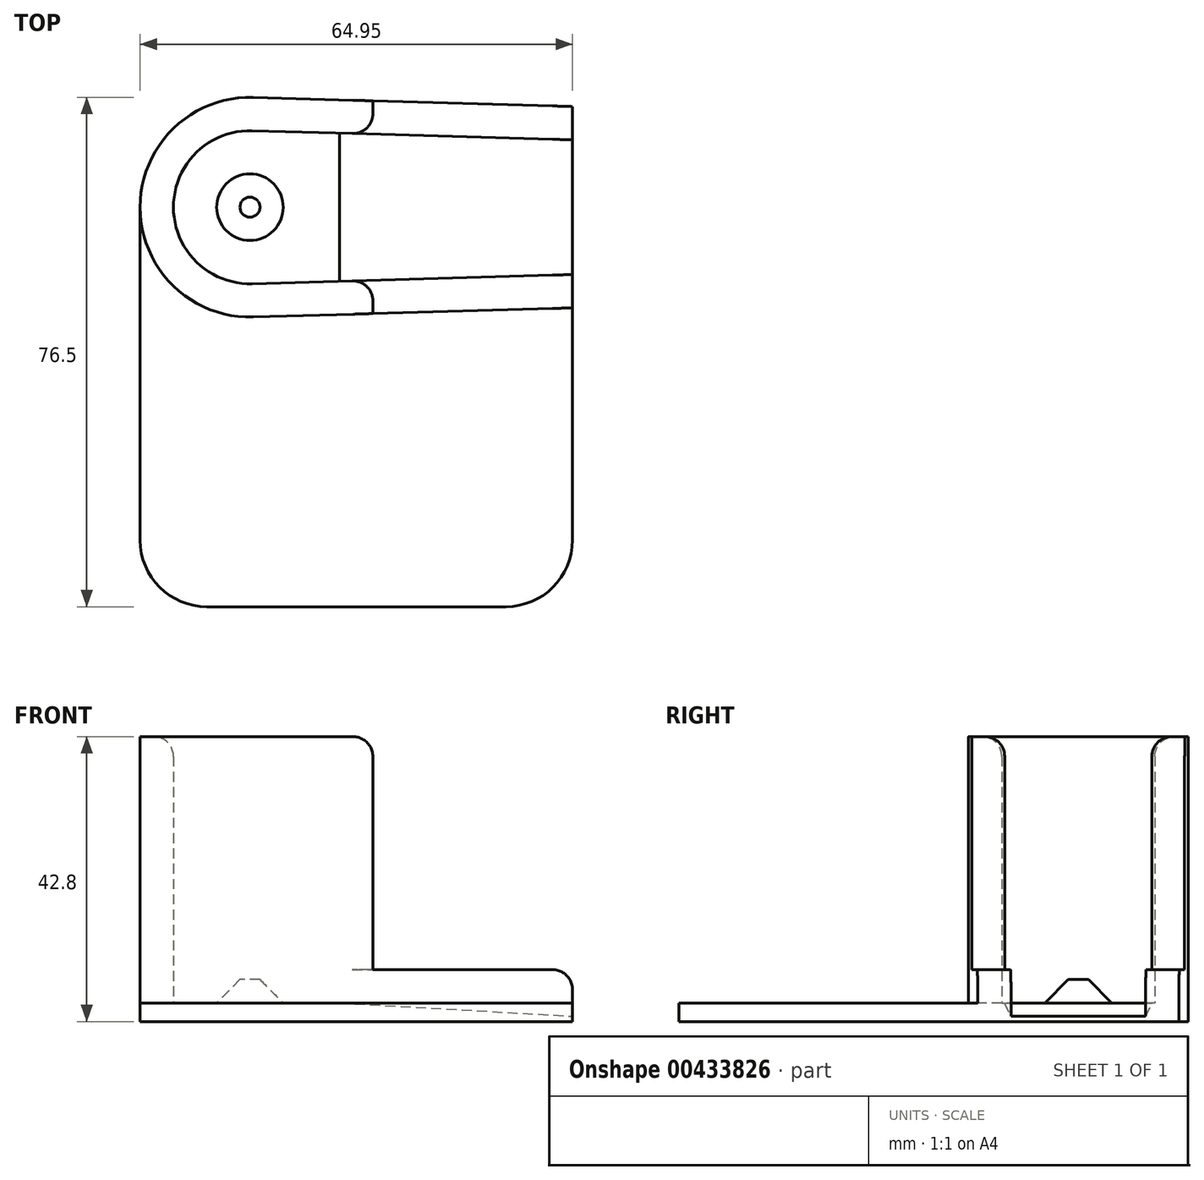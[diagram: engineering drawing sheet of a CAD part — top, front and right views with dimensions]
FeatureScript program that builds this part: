
annotation { "Feature Type Name" : "Feature", "Feature Type Description" : "" }
export const myFeature = defineFeature(function(context is Context, id is Id, definition is map)
    precondition{}
    {
        {
            var Q0;
            Q0=qCreatedBy(makeId("Top.planeOp"),FACE);
            var sketch = newSketch(context, id + "F0", { "sketchPlane" : qUnion([Q0])});
            skArc(sketch, "E0", {"start": v(0.54, 9.48) * mm, "mid": v(-9.5, 0.14) * mm, "end": v(0.27, -9.5) * mm, "construction": true});
            skCircle(sketch, "E1", {"center": v(122.1, 0) * mm, "radius": 6 * mm, "construction": true});
            skLineSegment(sketch, "E2", {"start": v(-9.5, 0) * mm, "end": v(128.1, 0) * mm, "construction": true});
            skLineSegment(sketch, "E3", {"start": v(0, 9.5) * mm, "end": v(122.27, 6) * mm, "construction": true});
            skLineSegment(sketch, "E4", {"start": v(122.27, -6) * mm, "end": v(0, -9.5) * mm, "construction": true});
            skArc(sketch, "E5.0", {"start": v(0.33, 11.5) * mm, "mid": v(-11.5, 0) * mm, "end": v(0.33, -11.5) * mm});
            skCircle(sketch, "E6.0", {"center": v(122.1, 0) * mm, "radius": 8 * mm, "construction": true});
            skLineSegment(sketch, "E7", {"start": v(0.33, 11.5) * mm, "end": v(18.47, 10.98) * mm});
            skLineSegment(sketch, "E8.MirrorCS", {"start": v(0.33, -11.5) * mm, "end": v(18.47, -10.98) * mm});
            skLineSegment(sketch, "E9.0", {"start": v(0.47, 16.5) * mm, "end": v(18.47, 15.98) * mm});
            skArc(sketch, "E9.1", {"start": v(0.47, 16.5) * mm, "mid": v(-16.5, 0) * mm, "end": v(0.47, -16.5) * mm});
            skLineSegment(sketch, "E9.2", {"start": v(0.47, -16.5) * mm, "end": v(18.47, -15.98) * mm});
            skLineSegment(sketch, "E10", {"start": v(18.47, 15.98) * mm, "end": v(18.47, -15.98) * mm, "construction": true});
            skLineSegment(sketch, "E11", {"start": v(18.47, 15.98) * mm, "end": v(18.47, 10.98) * mm});
            skLineSegment(sketch, "E12.MirrorCS", {"start": v(18.47, -15.98) * mm, "end": v(18.47, -10.98) * mm});
            skPoint(sketch, "E13.orphan", {"position": v(122.33, -8) * mm});
            skPoint(sketch, "E14.orphan", {"position": v(122.33, 8) * mm});
            skLineSegment(sketch, "E15", {"start": v(18.47, -15.98) * mm, "end": v(48.45, -15.12) * mm});
            skLineSegment(sketch, "E16", {"start": v(48.45, -15.12) * mm, "end": v(48.45, -10.12) * mm});
            skLineSegment(sketch, "E17", {"start": v(48.45, -10.12) * mm, "end": v(18.47, -10.98) * mm});
            skLineSegment(sketch, "E18.MirrorCS", {"start": v(48.45, 10.12) * mm, "end": v(18.47, 10.98) * mm});
            skLineSegment(sketch, "E19.MirrorCS", {"start": v(18.47, 15.98) * mm, "end": v(48.45, 15.12) * mm});
            skLineSegment(sketch, "E20.MirrorCS", {"start": v(48.45, 15.12) * mm, "end": v(48.45, 10.12) * mm});
            skLineSegment(sketch, "E21", {"start": v(-16.5, 0) * mm, "end": v(-16.5, -50) * mm});
            skLineSegment(sketch, "E22", {"start": v(-6.5, -60) * mm, "end": v(38.45, -60) * mm});
            skLineSegment(sketch, "E23", {"start": v(48.45, -50) * mm, "end": v(48.45, -15.12) * mm});
            skPoint(sketch, "E24.visualSharp", {"position": v(-16.5, -60) * mm});
            skArc(sketch, "E24.filletArc", {"start": v(-16.5, -50) * mm, "mid": v(-13.57, -57.07) * mm, "end": v(-6.5, -60) * mm});
            skPoint(sketch, "E25.visualSharp", {"position": v(48.45, -60) * mm});
            skArc(sketch, "E25.filletArc", {"start": v(38.45, -60) * mm, "mid": v(45.52, -57.07) * mm, "end": v(48.45, -50) * mm});
            skLineSegment(sketch, "E26", {"start": v(48.45, -10.12) * mm, "end": v(48.45, 10.12) * mm});
            skSolve(sketch);
        }
        {
            var Q0;
            Q0=makeQuery(id+"F0.imprint","IMPRINT",FACE,{"disambiguationData":[TD([[makeQuery(id+"F0.imprint","IMPRINT",EDGE,{"derivedFrom":sQuery(id+"F0.wireOp",EDGE,"E5.0")}),-1.0]])]});
            extrude(context, id + "F1", {"entities" : qUnion([Q0]), "depth" : 40 * mm});
        }
        {
            var Q0;
            Q0=makeQuery(id+"F0.imprint","IMPRINT",FACE,{"disambiguationData":[TD([[makeQuery(id+"F0.imprint","IMPRINT",EDGE,{"derivedFrom":sQuery(id+"F0.wireOp",EDGE,"E11")}),1.0]])]});
            var Q1;
            Q1=makeQuery(id+"F0.imprint","IMPRINT",FACE,{"disambiguationData":[TD([[makeQuery(id+"F0.imprint","IMPRINT",EDGE,{"derivedFrom":sQuery(id+"F0.wireOp",EDGE,"E12.MirrorCS")}),-1.0]])]});
            extrude(context, id + "F2", {"entities" : qUnion([Q0, Q1]), "operationType" : NewBodyOperationType.ADD, "depth" : 5 * mm});
        }
        {
            var Q0;
            Q0 = qSketchRegion(id + "F0", true);
            extrude(context, id + "F3", {"entities" : qUnion([Q0]), "operationType" : NewBodyOperationType.ADD, "oppositeDirection" : true, "depth" : 2.8 * mm});
        }
        {
            var Q0;
            Q0=makeQuery(id+"F0.imprint","IMPRINT",FACE,{"disambiguationData":[TD([[makeQuery(id+"F0.imprint","IMPRINT",EDGE,{"derivedFrom":sQuery(id+"F0.wireOp",EDGE,"E5.0")}),1.0]])]});
            var sketch = newSketch(context, id + "F4", { "sketchPlane" : qUnion([Q0])});
            skCircle(sketch, "E27", {"center": v(0, 0) * mm, "radius": 5 * mm});
            skSolve(sketch);
        }
        {
            var Q0;
            Q0=makeQuery(id+"F4.imprint","IMPRINT",FACE,{"disambiguationData":[TD([[makeQuery(id+"F4.imprint","IMPRINT",EDGE,{"derivedFrom":sQuery(id+"F4.wireOp",EDGE,"E27")}),1.0]])]});
            extrude(context, id + "F5", {"entities" : qUnion([Q0]), "operationType" : NewBodyOperationType.ADD, "depth" : 3.5 * mm, "hasDraft" : true, "draftAngle" : 45 * degree, "draftPullDirection" : true});
        }
        {
            var Q0;
            Q0=makeQuery(id+"F1.opExtrude","CAP_EDGE",EDGE,{"disambiguationData":[OSD([sQuery(id+"F0.wireOp",EDGE,"E12.MirrorCS")])],"isStart":false});
            var Q1;
            Q1=makeQuery(id+"F2.opExtrude","CAP_EDGE",EDGE,{"disambiguationData":[OSD([sQuery(id+"F0.wireOp",EDGE,"E12.MirrorCS")])],"isStart":false});
            var Q2;
            Q2=makeQuery(id+"F1.opExtrude","CAP_EDGE",EDGE,{"disambiguationData":[OSD([sQuery(id+"F0.wireOp",EDGE,"E11")])],"isStart":false});
            var Q3;
            Q3=makeQuery(id+"F2.opExtrude","CAP_EDGE",EDGE,{"disambiguationData":[OSD([sQuery(id+"F0.wireOp",EDGE,"E11")])],"isStart":false});
            var Q4;
            Q4=makeQuery(id+"F2.opExtrude","CAP_EDGE",EDGE,{"disambiguationData":[OSD([sQuery(id+"F0.wireOp",EDGE,"E16")])],"isStart":false});
            var Q5;
            Q5=makeQuery(id+"F2.opExtrude","CAP_EDGE",EDGE,{"disambiguationData":[OSD([sQuery(id+"F0.wireOp",EDGE,"E20.MirrorCS")])],"isStart":false});
            var Q6;
            Q6=makeQuery(id+"F1.opExtrude","SWEPT_EDGE",EDGE,{"disambiguationData":[OSD([sQuery(id+"F0.wireOp",EDGE,"E8.MirrorCS"),sQuery(id+"F0.wireOp",EDGE,"E12.MirrorCS"),sQuery(id+"F0.wireOp",EDGE,"E17")])]});
            var Q7;
            Q7=makeQuery(id+"F1.opExtrude","CAP_EDGE",EDGE,{"disambiguationData":[OSD([sQuery(id+"F0.wireOp",EDGE,"E8.MirrorCS")])],"isStart":false});
            var Q8;
            Q8=makeQuery(id+"F1.opExtrude","SWEPT_EDGE",EDGE,{"disambiguationData":[OSD([sQuery(id+"F0.wireOp",EDGE,"E7"),sQuery(id+"F0.wireOp",EDGE,"E11"),sQuery(id+"F0.wireOp",EDGE,"E18.MirrorCS")])]});
            fillet(context, id + "F6", {"entities" : qUnion([Q0, Q1, Q2, Q3, Q4, Q5, Q6, Q7, Q8]), "radius" : 3 * mm, "tangentPropagation" : true, "allowEdgeOverflow" : false});
        }
        {
            var Q0;
            {var subQ0=sQuery(id+"F0.wireOp",EDGE,"E26");var subQ1=sQuery(id+"F0.wireOp",EDGE,"E23");var subQ2=sQuery(id+"F0.wireOp",EDGE,"E20.MirrorCS");var subQ3=sQuery(id+"F0.wireOp",EDGE,"E16");Q0=makeQuery(id+"F3.boolean.opBoolean","SPLIT",EDGE,{"disambiguationData":[TD([makeQuery(id+"F1.opExtrude","SWEPT_FACE",FACE,{"disambiguationData":[OSD([sQuery(id+"F0.wireOp",EDGE,"E7")])]})])],"derivedFrom":makeQuery(id+"F3.opExtrude","CAP_EDGE",EDGE,{"disambiguationData":[OSD([subQ3,subQ2,subQ1,subQ0])],"isStart":true})});}
            chamfer(context, id + "F7", {"entities" : qUnion([Q0]), "chamferType" : ChamferType.TWO_OFFSETS, "width1" : 35 * mm, "oppositeDirection" : false, "width2" : 2 * mm, "tangentPropagation" : true});
        }
    });
